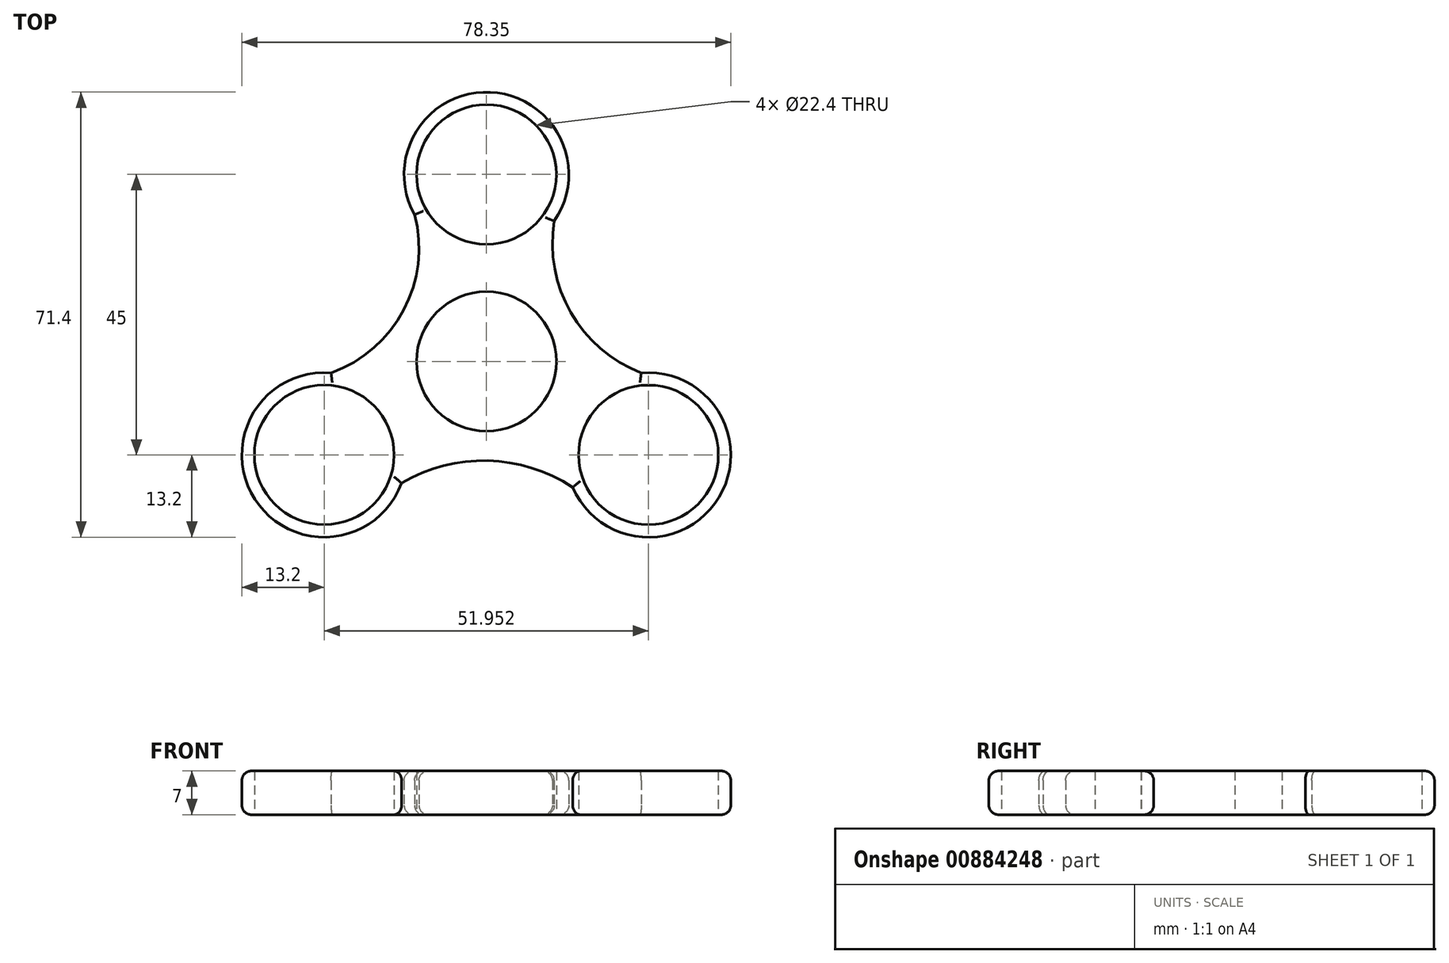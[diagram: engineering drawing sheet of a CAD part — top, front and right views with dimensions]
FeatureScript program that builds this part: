
annotation { "Feature Type Name" : "Feature", "Feature Type Description" : "" }
export const myFeature = defineFeature(function(context is Context, id is Id, definition is map)
    precondition{}
    {
        {
            var Q0;
            Q0=qCreatedBy(makeId("Top.planeOp"),FACE);
            var sketch = newSketch(context, id + "F0", { "sketchPlane" : qUnion([Q0])});
            skCircle(sketch, "E0", {"center": v(0, 0) * mm, "radius": 11.2 * mm});
            skCircle(sketch, "E1", {"center": v(0, 30) * mm, "radius": 11.2 * mm});
            skArc(sketch, "E2", {"start": v(10.87, 22.51) * mm, "mid": v(0.6, 43.19) * mm, "end": v(-11.51, 23.55) * mm});
            skArc(sketch, "E3.1.0", {"start": v(-24.9, -1.83) * mm, "mid": v(-37.11, -22.1) * mm, "end": v(-13.6, -19.51) * mm});
            skCircle(sketch, "E3.1.1", {"center": v(-26, -14.98) * mm, "radius": 11.2 * mm});
            skArc(sketch, "E3.2.0", {"start": v(13.82, -20.19) * mm, "mid": v(37.29, -21.78) * mm, "end": v(24.8, -1.85) * mm});
            skCircle(sketch, "E3.2.1", {"center": v(25.96, -15) * mm, "radius": 11.2 * mm});
            skLineSegment(sketch, "E4", {"start": v(-11.4, -6.64) * mm, "end": v(-9.67, -5.65) * mm, "construction": true});
            skArc(sketch, "E5", {"start": v(10.87, 22.51) * mm, "mid": v(13.52, 7.86) * mm, "end": v(24.8, -1.85) * mm});
            skArc(sketch, "E6", {"start": v(13.82, -20.19) * mm, "mid": v(0.21, -15.92) * mm, "end": v(-13.6, -19.51) * mm});
            skArc(sketch, "E7", {"start": v(-24.9, -1.83) * mm, "mid": v(-13.26, 8.25) * mm, "end": v(-11.51, 23.55) * mm});
            skSolve(sketch);
        }
        {
            var Q0;
            Q0=makeQuery(id+"F0.imprint","IMPRINT",FACE,{"disambiguationData":[TD([[makeQuery(id+"F0.imprint","IMPRINT",EDGE,{"derivedFrom":sQuery(id+"F0.wireOp",EDGE,"E0")}),-1.0]])]});
            extrude(context, id + "F1", {"entities" : qUnion([Q0]), "depth" : 7 * mm, "offsetDistance" : 25 * mm});
        }
        {
            var Q0;
            Q0=makeQuery(id+"F1.opExtrude","CAP_EDGE",EDGE,{"disambiguationData":[OSD([sQuery(id+"F0.wireOp",EDGE,"E6")])],"isStart":true});
            var Q1;
            Q1=makeQuery(id+"F1.opExtrude","CAP_EDGE",EDGE,{"disambiguationData":[OSD([sQuery(id+"F0.wireOp",EDGE,"E3.2.0")])],"isStart":true});
            var Q2;
            Q2=makeQuery(id+"F1.opExtrude","CAP_EDGE",EDGE,{"disambiguationData":[OSD([sQuery(id+"F0.wireOp",EDGE,"E5")])],"isStart":true});
            var Q3;
            Q3=makeQuery(id+"F1.opExtrude","CAP_EDGE",EDGE,{"disambiguationData":[OSD([sQuery(id+"F0.wireOp",EDGE,"E2")])],"isStart":true});
            var Q4;
            Q4=makeQuery(id+"F1.opExtrude","CAP_EDGE",EDGE,{"disambiguationData":[OSD([sQuery(id+"F0.wireOp",EDGE,"E7")])],"isStart":true});
            var Q5;
            Q5=makeQuery(id+"F1.opExtrude","CAP_EDGE",EDGE,{"disambiguationData":[OSD([sQuery(id+"F0.wireOp",EDGE,"E3.1.0")])],"isStart":true});
            var Q6;
            Q6=makeQuery(id+"F1.opExtrude","CAP_EDGE",EDGE,{"disambiguationData":[OSD([sQuery(id+"F0.wireOp",EDGE,"E3.2.0")])],"isStart":false});
            var Q7;
            Q7=makeQuery(id+"F1.opExtrude","CAP_EDGE",EDGE,{"disambiguationData":[OSD([sQuery(id+"F0.wireOp",EDGE,"E5")])],"isStart":false});
            var Q8;
            Q8=makeQuery(id+"F1.opExtrude","CAP_EDGE",EDGE,{"disambiguationData":[OSD([sQuery(id+"F0.wireOp",EDGE,"E2")])],"isStart":false});
            var Q9;
            Q9=makeQuery(id+"F1.opExtrude","CAP_EDGE",EDGE,{"disambiguationData":[OSD([sQuery(id+"F0.wireOp",EDGE,"E3.1.0")])],"isStart":false});
            var Q10;
            Q10=makeQuery(id+"F1.opExtrude","CAP_EDGE",EDGE,{"disambiguationData":[OSD([sQuery(id+"F0.wireOp",EDGE,"E6")])],"isStart":false});
            var Q11;
            Q11=makeQuery(id+"F1.opExtrude","CAP_EDGE",EDGE,{"disambiguationData":[OSD([sQuery(id+"F0.wireOp",EDGE,"E7")])],"isStart":false});
            fillet(context, id + "F2", {"entities" : qUnion([Q0, Q1, Q2, Q3, Q4, Q5, Q6, Q7, Q8, Q9, Q10, Q11]), "radius" : 1.5 * mm, "tangentPropagation" : true, "allowEdgeOverflow" : false});
        }
    });
